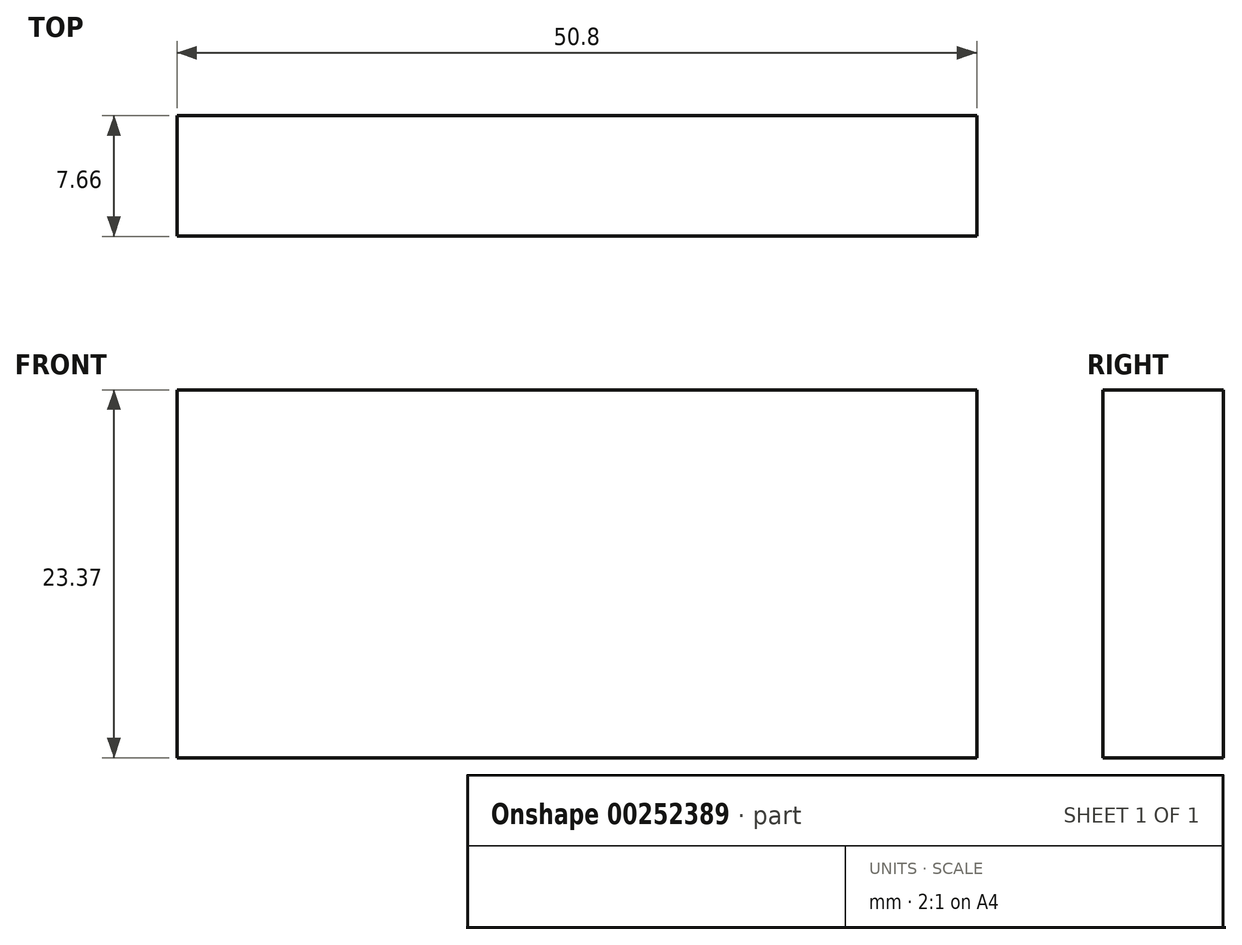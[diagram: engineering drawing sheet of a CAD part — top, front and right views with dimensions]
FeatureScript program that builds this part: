
annotation { "Feature Type Name" : "Feature", "Feature Type Description" : "" }
export const myFeature = defineFeature(function(context is Context, id is Id, definition is map)
    precondition{}
    {
        {
            var Q0;
            Q0=qCreatedBy(makeId("Front.planeOp"),FACE);
            var sketch = newSketch(context, id + "F0", { "sketchPlane" : qUnion([Q0])});
            skLineSegment(sketch, "E0.bottom", {"start": v(-55.84, 10.61) * mm, "end": v(-5.04, 10.61) * mm});
            skLineSegment(sketch, "E0.top", {"start": v(-55.84, -12.76) * mm, "end": v(-5.04, -12.76) * mm});
            skLineSegment(sketch, "E0.left", {"start": v(-55.84, 10.61) * mm, "end": v(-55.84, -12.76) * mm});
            skLineSegment(sketch, "E0.right", {"start": v(-5.04, 10.61) * mm, "end": v(-5.04, -12.76) * mm});
            skSolve(sketch);
        }
        {
            var Q0;
            Q0=makeQuery(id+"F0.imprint","IMPRINT",FACE,{"disambiguationData":[TD([[makeQuery(id+"F0.imprint","IMPRINT",EDGE,{"derivedFrom":sQuery(id+"F0.wireOp",EDGE,"E0.bottom")}),-1.0]])]});
            extrude(context, id + "F1", {"entities" : qUnion([Q0]), "endBound" : BoundingType.SYMMETRIC, "depth" : 7.65 * mm});
        }
    });
